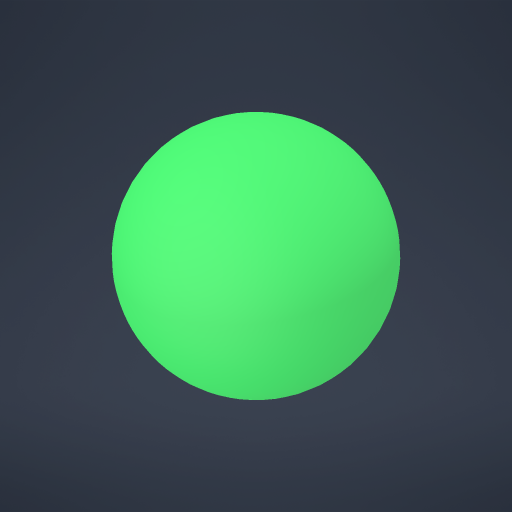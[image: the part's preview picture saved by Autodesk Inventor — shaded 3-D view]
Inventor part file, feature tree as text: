
AUTODESK INVENTOR PART (.ipt)
format: ipt  version: 2023.4 (Build 274418000, 418)  size: 194,560 bytes
history: native  units: in
note: dims shown in document units (in); Inventor stores cm internally (conversion verified against a paired STEP export)
features: revolve x1
ambient origin geometry x8: Origin, YZ Plane, XZ Plane, XY Plane, X Axis, Y Axis, Z Axis, Center Point
bodies: Solid1 (feature_tree)
feature tree (1):
  revolve  "Revolve2"  [1 undecoded]
note: 1 required parameter value undecoded (feature->parameter linkage not recoverable at this tier; creation-order binding heuristic only, values carry confidence <= 0.55)
